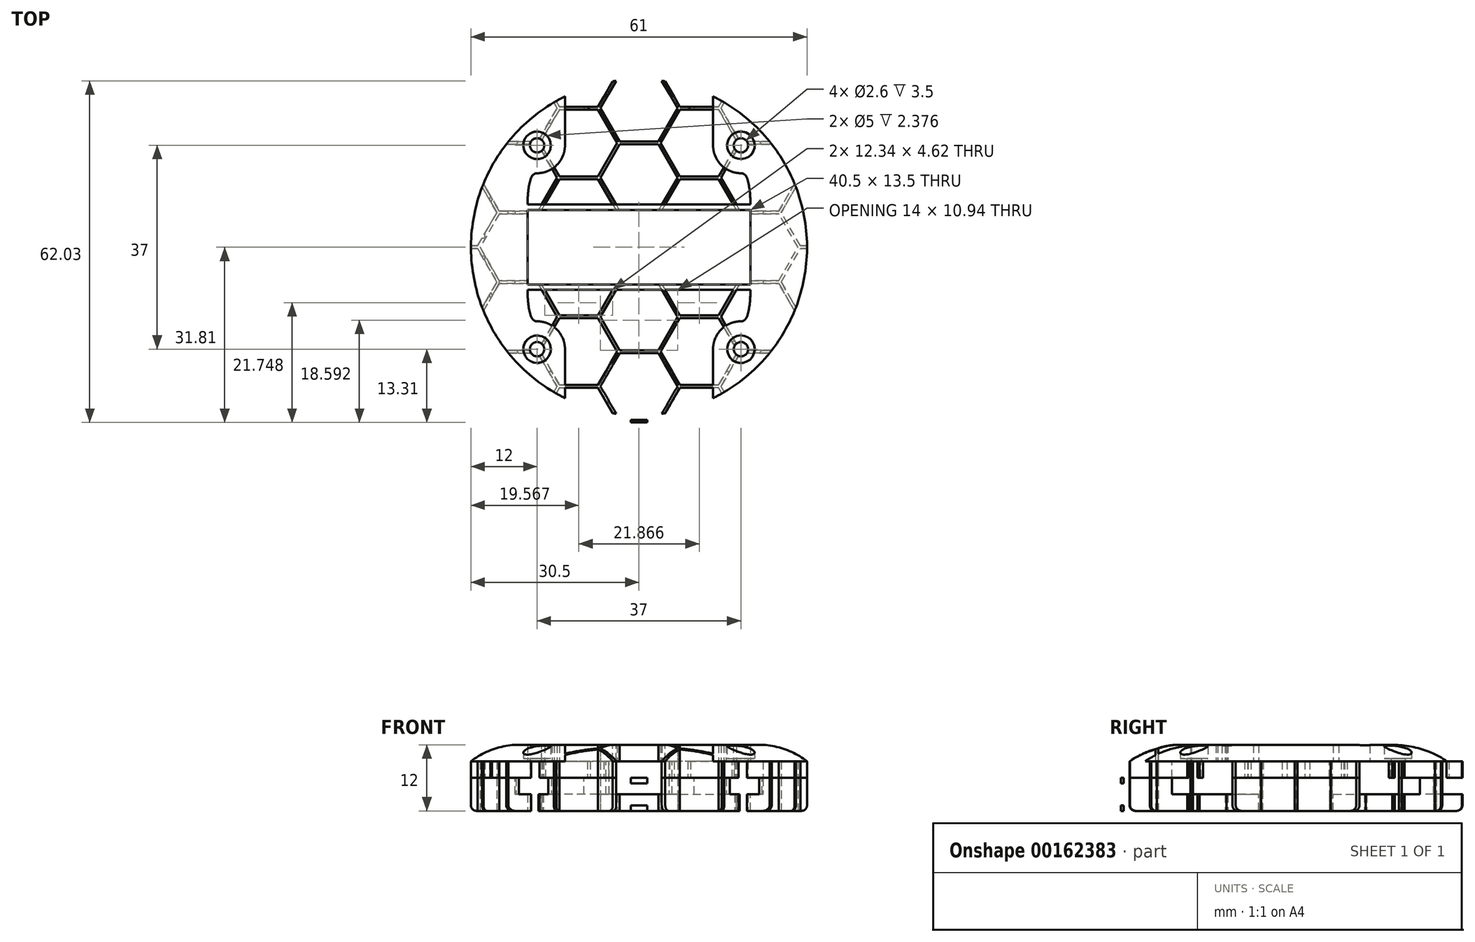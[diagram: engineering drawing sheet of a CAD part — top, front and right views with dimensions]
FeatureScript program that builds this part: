
annotation { "Feature Type Name" : "Feature", "Feature Type Description" : "" }
export const myFeature = defineFeature(function(context is Context, id is Id, definition is map)
    precondition{}
    {
        {
            var Q0;
            Q0=qCreatedBy(makeId("Top.planeOp"),FACE);
            var sketch = newSketch(context, id + "F0", { "sketchPlane" : qUnion([Q0])});
            skCircle(sketch, "E0", {"center": v(0, 0) * mm, "radius": 30.5 * mm});
            skLineSegment(sketch, "E1.bottom", {"start": v(18.5, 18.5) * mm, "end": v(-18.5, 18.5) * mm, "construction": true});
            skLineSegment(sketch, "E1.top", {"start": v(18.5, -18.5) * mm, "end": v(-18.5, -18.5) * mm, "construction": true});
            skLineSegment(sketch, "E1.left", {"start": v(18.5, 18.5) * mm, "end": v(18.5, -18.5) * mm, "construction": true});
            skLineSegment(sketch, "E1.right", {"start": v(-18.5, 18.5) * mm, "end": v(-18.5, -18.5) * mm, "construction": true});
            skCircle(sketch, "E2", {"center": v(-18.5, 18.5) * mm, "radius": 1.25 * mm});
            skCircle(sketch, "E3", {"center": v(18.5, 18.5) * mm, "radius": 1.25 * mm});
            skCircle(sketch, "E4", {"center": v(18.5, -18.5) * mm, "radius": 1.25 * mm});
            skCircle(sketch, "E5", {"center": v(-18.5, -18.5) * mm, "radius": 1.25 * mm});
            skLineSegment(sketch, "E6.bottom", {"start": v(22.5, 22.5) * mm, "end": v(-22.5, 22.5) * mm, "construction": true});
            skLineSegment(sketch, "E6.top", {"start": v(22.5, -22.5) * mm, "end": v(-22.5, -22.5) * mm, "construction": true});
            skLineSegment(sketch, "E6.left", {"start": v(22.5, 22.5) * mm, "end": v(22.5, -22.5) * mm, "construction": true});
            skLineSegment(sketch, "E6.right", {"start": v(-22.5, 22.5) * mm, "end": v(-22.5, -22.5) * mm, "construction": true});
            skLineSegment(sketch, "E7", {"start": v(-18.5, 22.5) * mm, "end": v(-22.5, 18.5) * mm});
            skLineSegment(sketch, "E8", {"start": v(-22.5, 18.5) * mm, "end": v(-22.5, -18.5) * mm});
            skLineSegment(sketch, "E9", {"start": v(-22.5, -18.5) * mm, "end": v(-18.5, -22.5) * mm});
            skLineSegment(sketch, "E10", {"start": v(-18.5, -22.5) * mm, "end": v(18.5, -22.5) * mm});
            skLineSegment(sketch, "E11", {"start": v(18.5, -22.5) * mm, "end": v(22.5, -18.5) * mm});
            skLineSegment(sketch, "E12", {"start": v(22.5, -18.5) * mm, "end": v(22.5, 18.5) * mm});
            skLineSegment(sketch, "E13", {"start": v(22.5, 18.5) * mm, "end": v(18.5, 22.5) * mm});
            skLineSegment(sketch, "E14", {"start": v(-18.5, 22.5) * mm, "end": v(18.5, 22.5) * mm});
            skLineSegment(sketch, "E15", {"start": v(-22.5, 22.5) * mm, "end": v(22.5, -22.5) * mm, "construction": true});
            skLineSegment(sketch, "E16", {"start": v(-22.5, -22.5) * mm, "end": v(22.5, 22.5) * mm, "construction": true});
            skLineSegment(sketch, "E17", {"start": v(-10, 22.5) * mm, "end": v(-10, 28.81) * mm});
            skLineSegment(sketch, "E18", {"start": v(10, 22.5) * mm, "end": v(10, 28.81) * mm});
            skSolve(sketch);
        }
        {
            var Q0;
            Q0=makeQuery(id+"F0.imprint","IMPRINT",FACE,{"disambiguationData":[TD([[makeQuery(id+"F0.imprint","IMPRINT",EDGE,{"derivedFrom":sQuery(id+"F0.wireOp",EDGE,"E2")}),-1.0]])]});
            var Q1;
            {var subQ4=sQuery(id+"F0.wireOp",EDGE,"E7");Q1=makeQuery(id+"F0.imprint","IMPRINT",FACE,{"disambiguationData":[TD([[makeQuery(id+"F0.imprint","IMPRINT",EDGE,{"derivedFrom":subQ4}),-1.0]])]});}
            var Q2;
            {var subQ0=sQuery(id+"F0.wireOp",EDGE,"E17");Q2=makeQuery(id+"F0.imprint","IMPRINT",FACE,{"disambiguationData":[TD([[makeQuery(id+"F0.imprint","IMPRINT",EDGE,{"derivedFrom":subQ0}),-1.0]])]});}
            extrude(context, id + "F1", {"entities" : qUnion([Q0, Q1, Q2]), "depth" : 3 * mm});
        }
        {
            var Q0;
            {var subQ4=sQuery(id+"F0.wireOp",EDGE,"E7");Q0=makeQuery(id+"F0.imprint","IMPRINT",FACE,{"disambiguationData":[TD([[makeQuery(id+"F0.imprint","IMPRINT",EDGE,{"derivedFrom":subQ4}),-1.0]])]});}
            extrude(context, id + "F2", {"entities" : qUnion([Q0]), "operationType" : NewBodyOperationType.ADD, "depth" : 6 * mm});
        }
        {
            var Q0;
            Q0=qCreatedBy(makeId("Right.planeOp"),FACE);
            var sketch = newSketch(context, id + "F3", { "sketchPlane" : qUnion([Q0])});
            skLineSegment(sketch, "E19.bottom", {"start": v(-29, 0) * mm, "end": v(-36.5, 0) * mm});
            skLineSegment(sketch, "E19.top", {"start": v(-29, 6) * mm, "end": v(-36.5, 6) * mm});
            skLineSegment(sketch, "E19.left", {"start": v(-29, 0) * mm, "end": v(-29, 6) * mm});
            skLineSegment(sketch, "E19.right", {"start": v(-36.5, 0) * mm, "end": v(-36.5, 6) * mm});
            skLineSegment(sketch, "E20.bottom", {"start": v(-29, 1) * mm, "end": v(-35, 1) * mm});
            skLineSegment(sketch, "E20.top", {"start": v(-29, 5) * mm, "end": v(-35, 5) * mm});
            skLineSegment(sketch, "E20.left", {"start": v(-29, 1) * mm, "end": v(-29, 5) * mm});
            skLineSegment(sketch, "E20.right", {"start": v(-35, 1) * mm, "end": v(-35, 5) * mm});
            skSolve(sketch);
        }
        {
            var Q0;
            {var subQ4=sQuery(id+"F3.wireOp",EDGE,"E19.bottom");Q0=makeQuery(id+"F3.imprint","IMPRINT",FACE,{"disambiguationData":[TD([[makeQuery(id+"F3.imprint","IMPRINT",EDGE,{"derivedFrom":subQ4}),-1.0]])]});}
            extrude(context, id + "F4", {"entities" : qUnion([Q0]), "operationType" : NewBodyOperationType.ADD, "depth" : 1.5 * mm, "hasSecondDirection" : true, "secondDirectionOppositeDirection" : true, "secondDirectionDepth" : 1.5 * mm});
        }
        {
            var Q0;
            Q0=makeQuery(id+"F1.opExtrude","CAP_EDGE",EDGE,{"disambiguationData":[OSD([sQuery(id+"F0.wireOp",EDGE,"E0")])],"isStart":true});
            fillet(context, id + "F5", {"entities" : qUnion([Q0]), "radius" : 1 * mm, "tangentPropagation" : true, "allowEdgeOverflow" : false});
        }
        {
            var Q0;
            Q0=qCreatedBy(makeId("Top.planeOp"),FACE);
            var sketch = newSketch(context, id + "F6", { "sketchPlane" : qUnion([Q0])});
            skCircle(sketch, "E21", {"center": v(0, 0) * mm, "radius": 30.5 * mm});
            skLineSegment(sketch, "E22.bottom", {"start": v(18.5, 18.5) * mm, "end": v(-18.5, 18.5) * mm, "construction": true});
            skLineSegment(sketch, "E22.top", {"start": v(18.5, -18.5) * mm, "end": v(-18.5, -18.5) * mm, "construction": true});
            skLineSegment(sketch, "E22.left", {"start": v(18.5, 18.5) * mm, "end": v(18.5, -18.5) * mm, "construction": true});
            skLineSegment(sketch, "E22.right", {"start": v(-18.5, 18.5) * mm, "end": v(-18.5, -18.5) * mm, "construction": true});
            skCircle(sketch, "E23", {"center": v(-18.5, 18.5) * mm, "radius": 1.3 * mm});
            skCircle(sketch, "E24", {"center": v(18.5, 18.5) * mm, "radius": 1.3 * mm});
            skCircle(sketch, "E25", {"center": v(18.5, -18.5) * mm, "radius": 1.3 * mm});
            skCircle(sketch, "E26", {"center": v(-18.5, -18.5) * mm, "radius": 1.3 * mm});
            skLineSegment(sketch, "E27", {"start": v(-22.5, 15.67) * mm, "end": v(-22.5, -15.67) * mm});
            skLineSegment(sketch, "E28", {"start": v(-15.67, -22.5) * mm, "end": v(15.67, -22.5) * mm});
            skLineSegment(sketch, "E29", {"start": v(22.5, -15.67) * mm, "end": v(22.5, 15.67) * mm});
            skLineSegment(sketch, "E30", {"start": v(-15.67, 22.5) * mm, "end": v(-11.25, 22.5) * mm});
            skLineSegment(sketch, "E31", {"start": v(-22.5, 22.5) * mm, "end": v(22.5, -22.5) * mm, "construction": true});
            skLineSegment(sketch, "E32", {"start": v(-22.5, -22.5) * mm, "end": v(22.5, 22.5) * mm, "construction": true});
            skLineSegment(sketch, "E33", {"start": v(22.5, -15.67) * mm, "end": v(18.5, -15.67) * mm});
            skLineSegment(sketch, "E34", {"start": v(18.5, -15.67) * mm, "end": v(15.67, -18.5) * mm});
            skLineSegment(sketch, "E35", {"start": v(15.67, -18.5) * mm, "end": v(15.67, -22.5) * mm});
            skLineSegment(sketch, "E36", {"start": v(22.5, 15.67) * mm, "end": v(18.5, 15.67) * mm});
            skLineSegment(sketch, "E37", {"start": v(18.5, 15.67) * mm, "end": v(15.67, 18.5) * mm});
            skLineSegment(sketch, "E38", {"start": v(15.67, 18.5) * mm, "end": v(15.67, 22.5) * mm});
            skLineSegment(sketch, "E39", {"start": v(-15.67, -22.5) * mm, "end": v(-15.67, -18.5) * mm});
            skLineSegment(sketch, "E40", {"start": v(-15.67, -18.5) * mm, "end": v(-18.5, -15.67) * mm});
            skLineSegment(sketch, "E41", {"start": v(-18.5, -15.67) * mm, "end": v(-22.5, -15.67) * mm});
            skLineSegment(sketch, "E42", {"start": v(-15.67, 22.5) * mm, "end": v(-15.67, 18.5) * mm});
            skLineSegment(sketch, "E43", {"start": v(-15.67, 18.5) * mm, "end": v(-18.5, 15.67) * mm});
            skLineSegment(sketch, "E44", {"start": v(-18.5, 15.67) * mm, "end": v(-22.5, 15.67) * mm});
            skLineSegment(sketch, "E45.bottom", {"start": v(-20.25, -6.75) * mm, "end": v(20.25, -6.75) * mm});
            skLineSegment(sketch, "E45.top", {"start": v(-20.25, 6.75) * mm, "end": v(20.25, 6.75) * mm});
            skLineSegment(sketch, "E45.left", {"start": v(-20.25, -6.75) * mm, "end": v(-20.25, 6.75) * mm});
            skLineSegment(sketch, "E45.right", {"start": v(20.25, -6.75) * mm, "end": v(20.25, 6.75) * mm});
            skLineSegment(sketch, "E46.bottom", {"start": v(-22.5, -22.5) * mm, "end": v(22.5, -22.5) * mm, "construction": true});
            skLineSegment(sketch, "E46.left", {"start": v(-22.5, -22.5) * mm, "end": v(-22.5, 22.5) * mm, "construction": true});
            skLineSegment(sketch, "E46.right", {"start": v(22.5, -22.5) * mm, "end": v(22.5, 22.5) * mm, "construction": true});
            skArc(sketch, "E47", {"start": v(11.25, 22.5) * mm, "mid": v(0, 29) * mm, "end": v(-11.25, 22.5) * mm});
            skPoint(sketch, "E48", {"position": v(0, 18.5) * mm});
            skLineSegment(sketch, "E49.trimOffspring", {"start": v(11.25, 22.5) * mm, "end": v(15.67, 22.5) * mm});
            skCircle(sketch, "E50", {"center": v(18.5, 18.5) * mm, "radius": 2.5 * mm});
            skCircle(sketch, "E51", {"center": v(-18.5, 18.5) * mm, "radius": 2.5 * mm});
            skCircle(sketch, "E52", {"center": v(-18.5, -18.5) * mm, "radius": 2.5 * mm});
            skCircle(sketch, "E53", {"center": v(18.5, -18.5) * mm, "radius": 2.5 * mm});
            skLineSegment(sketch, "E54.bottom", {"start": v(-30.43, -2) * mm, "end": v(-28.43, -2) * mm});
            skLineSegment(sketch, "E54.top", {"start": v(-30.43, 2) * mm, "end": v(-28.43, 2) * mm});
            skPoint(sketch, "E54.middle", {"position": v(-28.43, 0) * mm});
            skPoint(sketch, "E54.middle.positionSnap0", {"position": v(-20.25, 0) * mm});
            skPoint(sketch, "E54.centerSnap0", {"position": v(-20.25, 0) * mm});
            skArc(sketch, "E55", {"start": v(-28.43, -2) * mm, "mid": v(-27.85, -6.06) * mm, "end": v(-26.69, -10) * mm});
            skArc(sketch, "E56", {"start": v(-28.43, 2) * mm, "mid": v(-27.45, 7.66) * mm, "end": v(-25.36, 13) * mm});
            skLineSegment(sketch, "E57", {"start": v(-25.36, 13) * mm, "end": v(-22.5, 13) * mm});
            skLineSegment(sketch, "E58", {"start": v(-22.5, 13) * mm, "end": v(-22.5, 10.14) * mm});
            skLineSegment(sketch, "E59", {"start": v(-22.5, 12.8) * mm, "end": v(-25.02, 12.8) * mm});
            skArc(sketch, "E60", {"start": v(-25.02, 12.8) * mm, "mid": v(-28.06, 1.53) * mm, "end": v(-26.26, -10) * mm});
            skLineSegment(sketch, "E61", {"start": v(-26.69, -10) * mm, "end": v(-26.26, -10) * mm});
            skLineSegment(sketch, "E62", {"start": v(-28.05, -1.6) * mm, "end": v(-31.71, -1.6) * mm});
            skLineSegment(sketch, "E63", {"start": v(-28.05, 1.6) * mm, "end": v(-31.71, 1.6) * mm});
            skArc(sketch, "E64", {"start": v(-31.71, -1.6) * mm, "mid": v(-33.31, 0) * mm, "end": v(-31.71, 1.6) * mm});
            skArc(sketch, "E65", {"start": v(-22.5, 10.14) * mm, "mid": v(-25.08, 0.24) * mm, "end": v(-25.14, -10) * mm});
            skLineSegment(sketch, "E66", {"start": v(-25.14, -10) * mm, "end": v(-22.5, -10) * mm});
            skSolve(sketch);
        }
        {
            var Q0;
            Q0=makeQuery(id+"F6.imprint","IMPRINT",FACE,{"disambiguationData":[TD([[makeQuery(id+"F6.imprint","IMPRINT",EDGE,{"derivedFrom":sQuery(id+"F6.wireOp",EDGE,"E21")}),1.0]])]});
            var Q1;
            Q1=makeQuery(id+"F6.imprint","IMPRINT",FACE,{"disambiguationData":[TD([[makeQuery(id+"F6.imprint","IMPRINT",EDGE,{"derivedFrom":sQuery(id+"F6.wireOp",EDGE,"E25")}),-1.0]])]});
            var Q2;
            Q2=makeQuery(id+"F6.imprint","IMPRINT",FACE,{"disambiguationData":[TD([[makeQuery(id+"F6.imprint","IMPRINT",EDGE,{"derivedFrom":sQuery(id+"F6.wireOp",EDGE,"E26")}),-1.0]])]});
            var Q3;
            Q3=makeQuery(id+"F6.imprint","IMPRINT",FACE,{"disambiguationData":[TD([[makeQuery(id+"F6.imprint","IMPRINT",EDGE,{"derivedFrom":sQuery(id+"F6.wireOp",EDGE,"E23")}),-1.0]])]});
            var Q4;
            Q4=makeQuery(id+"F6.imprint","IMPRINT",FACE,{"disambiguationData":[TD([[makeQuery(id+"F6.imprint","IMPRINT",EDGE,{"derivedFrom":sQuery(id+"F6.wireOp",EDGE,"E24")}),-1.0]])]});
            var Q5;
            {var subQ5=sQuery(id+"F6.wireOp",EDGE,"E64");Q5=makeQuery(id+"F6.imprint","IMPRINT",FACE,{"disambiguationData":[TD([[makeQuery(id+"F6.imprint","IMPRINT",EDGE,{"derivedFrom":subQ5}),-1.0]])]});}
            var Q6;
            Q6=makeQuery(id+"F6.imprint","IMPRINT",FACE,{"disambiguationData":[TD([[makeQuery(id+"F6.imprint","IMPRINT",EDGE,{"derivedFrom":sQuery(id+"F6.wireOp",EDGE,"E28")}),-1.0]])]});
            extrude(context, id + "F7", {"entities" : qUnion([Q0, Q1, Q2, Q3, Q4, Q5, Q6]), "depth" : 9 * mm, "hasSecondDirection" : true, "secondDirectionOppositeDirection" : false, "secondDirectionDepth" : 6 * mm});
        }
        {
            var Q0;
            Q0=qCreatedBy(makeId("Right.planeOp"),FACE);
            var sketch = newSketch(context, id + "F8", { "sketchPlane" : qUnion([Q0])});
            skLineSegment(sketch, "E67", {"start": v(30.5, 9) * mm, "end": v(30.5, 19.06) * mm});
            skLineSegment(sketch, "E68", {"start": v(30.5, 19.06) * mm, "end": v(-30.5, 19.06) * mm});
            skLineSegment(sketch, "E69", {"start": v(-30.5, 19.06) * mm, "end": v(-30.5, 9) * mm});
            skArc(sketch, "E70", {"start": v(30.5, 9) * mm, "mid": v(26.39, 11.23) * mm, "end": v(21.77, 12) * mm});
            skArc(sketch, "E71.MirrorCS", {"start": v(-30.5, 9) * mm, "mid": v(-26.39, 11.23) * mm, "end": v(-21.77, 12) * mm});
            skLineSegment(sketch, "E72", {"start": v(-21.77, 12) * mm, "end": v(21.77, 12) * mm});
            skLineSegment(sketch, "E73", {"start": v(0, 12) * mm, "end": v(0, 19.06) * mm});
            skSolve(sketch);
        }
        {
            var Q0;
            Q0=qCreatedBy(makeId("Top.planeOp"),FACE);
            var sketch = newSketch(context, id + "F9", { "sketchPlane" : qUnion([Q0])});
            skLineSegment(sketch, "E74", {"start": v(20.25, 6.75) * mm, "end": v(20.25, -6.75) * mm});
            skCircle(sketch, "E75", {"center": v(0, 0) * mm, "radius": 30.5 * mm});
            skLineSegment(sketch, "E76.bottom", {"start": v(-18.5, -18.5) * mm, "end": v(18.5, -18.5) * mm, "construction": true});
            skLineSegment(sketch, "E76.top", {"start": v(-18.5, 18.5) * mm, "end": v(18.5, 18.5) * mm, "construction": true});
            skLineSegment(sketch, "E76.left", {"start": v(-18.5, -18.5) * mm, "end": v(-18.5, 18.5) * mm, "construction": true});
            skLineSegment(sketch, "E76.right", {"start": v(18.5, -18.5) * mm, "end": v(18.5, 18.5) * mm, "construction": true});
            skLineSegment(sketch, "E77", {"start": v(18.5, -18.5) * mm, "end": v(-18.5, 18.5) * mm, "construction": true});
            skLineSegment(sketch, "E78", {"start": v(18.5, 18.5) * mm, "end": v(-18.5, -18.5) * mm, "construction": true});
            skCircle(sketch, "E79", {"center": v(18.5, -18.5) * mm, "radius": 5.06 * mm, "construction": true});
            skFitSpline(sketch, "E80", {"points": [v(20.25, -6.75) * mm, v(19.9, -11.5) * mm, v(18.5, -13.44) * mm], "startDerivative": vector(0, -9.06) * mm, "endDerivative": vector(-6.35, 0) * mm});
            skLineSegment(sketch, "E81", {"start": v(13.44, -18.5) * mm, "end": v(13.44, -27.38) * mm});
            skArc(sketch, "E82", {"start": v(18.5, -13.44) * mm, "mid": v(14.92, -14.92) * mm, "end": v(13.44, -18.5) * mm});
            skArc(sketch, "E83.MirrorCS", {"start": v(18.5, 13.44) * mm, "mid": v(14.92, 14.92) * mm, "end": v(13.44, 18.5) * mm});
            skFitSpline(sketch, "E84.MirrorCS", {"points": [v(20.25, 6.75) * mm, v(19.9, 11.5) * mm, v(18.5, 13.44) * mm], "startDerivative": vector(0, 9.06) * mm, "endDerivative": vector(-6.35, 0) * mm});
            skLineSegment(sketch, "E85", {"start": v(13.44, 18.5) * mm, "end": v(13.44, 27.38) * mm});
            skLineSegment(sketch, "E86.MirrorCS", {"start": v(-13.44, -18.5) * mm, "end": v(-13.44, -27.38) * mm});
            skArc(sketch, "E87.MirrorCS", {"start": v(-18.5, -13.44) * mm, "mid": v(-14.92, -14.92) * mm, "end": v(-13.44, -18.5) * mm});
            skFitSpline(sketch, "E88.MirrorCS", {"points": [v(-20.25, -6.75) * mm, v(-19.9, -11.5) * mm, v(-18.5, -13.44) * mm], "startDerivative": vector(0, -9.06) * mm, "endDerivative": vector(6.35, 0) * mm});
            skLineSegment(sketch, "E89.MirrorCS", {"start": v(-13.44, 18.5) * mm, "end": v(-13.44, 27.38) * mm});
            skLineSegment(sketch, "E90.MirrorCS", {"start": v(-20.25, 6.75) * mm, "end": v(-20.25, -6.75) * mm});
            skFitSpline(sketch, "E91.MirrorCS", {"points": [v(-20.25, 6.75) * mm, v(-19.9, 11.5) * mm, v(-18.5, 13.44) * mm], "startDerivative": vector(0, 9.06) * mm, "endDerivative": vector(6.35, 0) * mm});
            skArc(sketch, "E92.MirrorCS", {"start": v(-18.5, 13.44) * mm, "mid": v(-14.92, 14.92) * mm, "end": v(-13.44, 18.5) * mm});
            skLineSegment(sketch, "E93", {"start": v(20.25, 6.75) * mm, "end": v(-20.25, 6.75) * mm});
            skLineSegment(sketch, "E94", {"start": v(-20.25, -6.75) * mm, "end": v(20.25, -6.75) * mm});
            skLineSegment(sketch, "E95", {"start": v(20.24, -7.75) * mm, "end": v(-20.24, -7.75) * mm});
            skLineSegment(sketch, "E96", {"start": v(-20.24, 7.75) * mm, "end": v(20.25, 7.75) * mm});
            skSolve(sketch);
        }
        {
            var Q0;
            Q0=qCreatedBy(makeId("Top.planeOp"),FACE);
            var sketch = newSketch(context, id + "F10", { "sketchPlane" : qUnion([Q0])});
            skCircle(sketch, "E97.cCircle", {"center": v(0, 0) * mm, "radius": 7 * mm, "construction": true});
            skLineSegment(sketch, "E97.0", {"start": v(-7, 0) * mm, "end": v(-3.5, 6.06) * mm});
            skLineSegment(sketch, "E97.1", {"start": v(-3.5, 6.06) * mm, "end": v(3.5, 6.06) * mm});
            skLineSegment(sketch, "E97.2", {"start": v(3.5, 6.06) * mm, "end": v(7, 0) * mm});
            skLineSegment(sketch, "E97.3", {"start": v(7, 0) * mm, "end": v(3.5, -6.06) * mm});
            skLineSegment(sketch, "E97.4", {"start": v(3.5, -6.06) * mm, "end": v(-3.5, -6.06) * mm});
            skLineSegment(sketch, "E97.5", {"start": v(-3.5, -6.06) * mm, "end": v(-7, 0) * mm});
            skLineSegment(sketch, "E98.0.1.0", {"start": v(-3.5, 18.69) * mm, "end": v(3.5, 18.69) * mm});
            skLineSegment(sketch, "E98.0.1.1", {"start": v(3.5, 6.56) * mm, "end": v(-3.5, 6.56) * mm});
            skLineSegment(sketch, "E98.0.1.2", {"start": v(-3.5, 6.56) * mm, "end": v(-7, 12.62) * mm});
            skLineSegment(sketch, "E98.0.1.3", {"start": v(-7, 12.62) * mm, "end": v(-3.5, 18.69) * mm});
            skLineSegment(sketch, "E98.0.1.4", {"start": v(3.5, 18.69) * mm, "end": v(7, 12.62) * mm});
            skLineSegment(sketch, "E98.0.1.5", {"start": v(7, 12.62) * mm, "end": v(3.5, 6.56) * mm});
            skLineSegment(sketch, "E98.0.2.0", {"start": v(-3.5, 31.31) * mm, "end": v(3.5, 31.31) * mm});
            skLineSegment(sketch, "E98.0.2.1", {"start": v(3.5, 19.19) * mm, "end": v(-3.5, 19.19) * mm});
            skLineSegment(sketch, "E98.0.2.2", {"start": v(-3.5, 19.19) * mm, "end": v(-7, 25.25) * mm});
            skLineSegment(sketch, "E98.0.2.3", {"start": v(-7, 25.25) * mm, "end": v(-3.5, 31.31) * mm});
            skLineSegment(sketch, "E98.0.2.4", {"start": v(3.5, 31.31) * mm, "end": v(7, 25.25) * mm});
            skLineSegment(sketch, "E98.0.2.5", {"start": v(7, 25.25) * mm, "end": v(3.5, 19.19) * mm});
            skLineSegment(sketch, "E98.0.3.0", {"start": v(-3.5, 43.94) * mm, "end": v(3.5, 43.94) * mm});
            skLineSegment(sketch, "E98.0.3.1", {"start": v(3.5, 31.81) * mm, "end": v(-3.5, 31.81) * mm});
            skLineSegment(sketch, "E98.0.3.2", {"start": v(-3.5, 31.81) * mm, "end": v(-7, 37.87) * mm});
            skLineSegment(sketch, "E98.0.3.3", {"start": v(-7, 37.87) * mm, "end": v(-3.5, 43.94) * mm});
            skLineSegment(sketch, "E98.0.3.4", {"start": v(3.5, 43.94) * mm, "end": v(7, 37.87) * mm});
            skLineSegment(sketch, "E98.0.3.5", {"start": v(7, 37.87) * mm, "end": v(3.5, 31.81) * mm});
            skLineSegment(sketch, "E98.direction1", {"start": v(-2.6, -6.06) * mm, "end": v(-3.5, -6.06) * mm, "construction": true});
            skLineSegment(sketch, "E98.direction2", {"start": v(-3.5, -6.06) * mm, "end": v(-3.5, 6.56) * mm, "construction": true});
            skLineSegment(sketch, "E99.0.1.0", {"start": v(3.5, -6.56) * mm, "end": v(7, -12.62) * mm});
            skLineSegment(sketch, "E99.0.1.1", {"start": v(7, -12.62) * mm, "end": v(3.5, -18.69) * mm});
            skLineSegment(sketch, "E99.0.1.2", {"start": v(-3.5, -6.56) * mm, "end": v(3.5, -6.56) * mm});
            skLineSegment(sketch, "E99.0.1.3", {"start": v(-7, -12.62) * mm, "end": v(-3.5, -6.56) * mm});
            skLineSegment(sketch, "E99.0.1.4", {"start": v(3.5, -18.69) * mm, "end": v(-3.5, -18.69) * mm});
            skLineSegment(sketch, "E99.0.1.5", {"start": v(-3.5, -18.69) * mm, "end": v(-7, -12.62) * mm});
            skLineSegment(sketch, "E99.0.1.6", {"start": v(-2.6, -18.69) * mm, "end": v(-3.5, -18.69) * mm, "construction": true});
            skLineSegment(sketch, "E99.0.2.0", {"start": v(3.5, -19.19) * mm, "end": v(7, -25.25) * mm});
            skLineSegment(sketch, "E99.0.2.1", {"start": v(7, -25.25) * mm, "end": v(3.5, -31.31) * mm});
            skLineSegment(sketch, "E99.0.2.2", {"start": v(-3.5, -19.19) * mm, "end": v(3.5, -19.19) * mm});
            skLineSegment(sketch, "E99.0.2.3", {"start": v(-7, -25.25) * mm, "end": v(-3.5, -19.19) * mm});
            skLineSegment(sketch, "E99.0.2.4", {"start": v(3.5, -31.31) * mm, "end": v(-3.5, -31.31) * mm});
            skLineSegment(sketch, "E99.0.2.5", {"start": v(-3.5, -31.31) * mm, "end": v(-7, -25.25) * mm});
            skLineSegment(sketch, "E99.0.2.6", {"start": v(-2.6, -31.31) * mm, "end": v(-3.5, -31.31) * mm, "construction": true});
            skLineSegment(sketch, "E99.0.3.0", {"start": v(3.5, -31.81) * mm, "end": v(7, -37.87) * mm});
            skLineSegment(sketch, "E99.0.3.1", {"start": v(7, -37.87) * mm, "end": v(3.5, -43.94) * mm});
            skLineSegment(sketch, "E99.0.3.2", {"start": v(-3.5, -31.81) * mm, "end": v(3.5, -31.81) * mm});
            skLineSegment(sketch, "E99.0.3.3", {"start": v(-7, -37.87) * mm, "end": v(-3.5, -31.81) * mm});
            skLineSegment(sketch, "E99.0.3.4", {"start": v(3.5, -43.94) * mm, "end": v(-3.5, -43.94) * mm});
            skLineSegment(sketch, "E99.0.3.5", {"start": v(-3.5, -43.94) * mm, "end": v(-7, -37.87) * mm});
            skLineSegment(sketch, "E99.0.3.6", {"start": v(-2.6, -43.94) * mm, "end": v(-3.5, -43.94) * mm, "construction": true});
            skLineSegment(sketch, "E99.direction1", {"start": v(-2.6, -6.06) * mm, "end": v(-2.7, -6.06) * mm, "construction": true});
            skLineSegment(sketch, "E99.direction2", {"start": v(-2.6, -6.06) * mm, "end": v(-2.6, -18.69) * mm, "construction": true});
            skCircle(sketch, "E100.cCircle", {"center": v(10.93, -44.19) * mm, "radius": 7 * mm, "construction": true});
            skLineSegment(sketch, "E100.0", {"start": v(3.93, -44.19) * mm, "end": v(7.43, -38.12) * mm});
            skLineSegment(sketch, "E100.1", {"start": v(7.43, -38.12) * mm, "end": v(14.43, -38.12) * mm});
            skLineSegment(sketch, "E100.2", {"start": v(14.43, -38.12) * mm, "end": v(17.93, -44.19) * mm});
            skLineSegment(sketch, "E100.3", {"start": v(17.93, -44.19) * mm, "end": v(14.43, -50.25) * mm});
            skLineSegment(sketch, "E100.4", {"start": v(14.43, -50.25) * mm, "end": v(7.43, -50.25) * mm});
            skLineSegment(sketch, "E100.5", {"start": v(7.43, -50.25) * mm, "end": v(3.93, -44.19) * mm});
            skLineSegment(sketch, "E101.0.1.0", {"start": v(3.93, -31.56) * mm, "end": v(7.43, -25.5) * mm});
            skLineSegment(sketch, "E101.0.1.1", {"start": v(17.93, -31.56) * mm, "end": v(14.43, -37.62) * mm});
            skLineSegment(sketch, "E101.0.1.2", {"start": v(7.43, -25.5) * mm, "end": v(14.43, -25.5) * mm});
            skLineSegment(sketch, "E101.0.1.3", {"start": v(14.43, -25.5) * mm, "end": v(17.93, -31.56) * mm});
            skLineSegment(sketch, "E101.0.1.4", {"start": v(14.43, -37.62) * mm, "end": v(7.43, -37.62) * mm});
            skLineSegment(sketch, "E101.0.1.5", {"start": v(7.43, -37.62) * mm, "end": v(3.93, -31.56) * mm});
            skLineSegment(sketch, "E101.0.2.0", {"start": v(3.93, -18.94) * mm, "end": v(7.43, -12.87) * mm});
            skLineSegment(sketch, "E101.0.2.1", {"start": v(17.93, -18.94) * mm, "end": v(14.43, -25) * mm});
            skLineSegment(sketch, "E101.0.2.2", {"start": v(7.43, -12.87) * mm, "end": v(14.43, -12.87) * mm});
            skLineSegment(sketch, "E101.0.2.3", {"start": v(14.43, -12.87) * mm, "end": v(17.93, -18.94) * mm});
            skLineSegment(sketch, "E101.0.2.4", {"start": v(14.43, -25) * mm, "end": v(7.43, -25) * mm});
            skLineSegment(sketch, "E101.0.2.5", {"start": v(7.43, -25) * mm, "end": v(3.93, -18.94) * mm});
            skLineSegment(sketch, "E101.0.3.0", {"start": v(3.93, -6.31) * mm, "end": v(7.43, -0.25) * mm});
            skLineSegment(sketch, "E101.0.3.1", {"start": v(17.93, -6.31) * mm, "end": v(14.43, -12.37) * mm});
            skLineSegment(sketch, "E101.0.3.2", {"start": v(7.43, -0.25) * mm, "end": v(14.43, -0.25) * mm});
            skLineSegment(sketch, "E101.0.3.3", {"start": v(14.43, -0.25) * mm, "end": v(17.93, -6.31) * mm});
            skLineSegment(sketch, "E101.0.3.4", {"start": v(14.43, -12.37) * mm, "end": v(7.43, -12.37) * mm});
            skLineSegment(sketch, "E101.0.3.5", {"start": v(7.43, -12.37) * mm, "end": v(3.93, -6.31) * mm});
            skLineSegment(sketch, "E101.0.4.0", {"start": v(3.93, 6.31) * mm, "end": v(7.43, 12.37) * mm});
            skLineSegment(sketch, "E101.0.4.1", {"start": v(17.93, 6.31) * mm, "end": v(14.43, 0.25) * mm});
            skLineSegment(sketch, "E101.0.4.2", {"start": v(7.43, 12.37) * mm, "end": v(14.43, 12.37) * mm});
            skLineSegment(sketch, "E101.0.4.3", {"start": v(14.43, 12.37) * mm, "end": v(17.93, 6.31) * mm});
            skLineSegment(sketch, "E101.0.4.4", {"start": v(14.43, 0.25) * mm, "end": v(7.43, 0.25) * mm});
            skLineSegment(sketch, "E101.0.4.5", {"start": v(7.43, 0.25) * mm, "end": v(3.93, 6.31) * mm});
            skLineSegment(sketch, "E101.0.5.0", {"start": v(3.93, 18.94) * mm, "end": v(7.43, 25) * mm});
            skLineSegment(sketch, "E101.0.5.1", {"start": v(17.93, 18.94) * mm, "end": v(14.43, 12.87) * mm});
            skLineSegment(sketch, "E101.0.5.2", {"start": v(7.43, 25) * mm, "end": v(14.43, 25) * mm});
            skLineSegment(sketch, "E101.0.5.3", {"start": v(14.43, 25) * mm, "end": v(17.93, 18.94) * mm});
            skLineSegment(sketch, "E101.0.5.4", {"start": v(14.43, 12.87) * mm, "end": v(7.43, 12.87) * mm});
            skLineSegment(sketch, "E101.0.5.5", {"start": v(7.43, 12.87) * mm, "end": v(3.93, 18.94) * mm});
            skLineSegment(sketch, "E101.0.6.0", {"start": v(3.93, 31.56) * mm, "end": v(7.43, 37.62) * mm});
            skLineSegment(sketch, "E101.0.6.1", {"start": v(17.93, 31.56) * mm, "end": v(14.43, 25.5) * mm});
            skLineSegment(sketch, "E101.0.6.2", {"start": v(7.43, 37.62) * mm, "end": v(14.43, 37.62) * mm});
            skLineSegment(sketch, "E101.0.6.3", {"start": v(14.43, 37.62) * mm, "end": v(17.93, 31.56) * mm});
            skLineSegment(sketch, "E101.0.6.4", {"start": v(14.43, 25.5) * mm, "end": v(7.43, 25.5) * mm});
            skLineSegment(sketch, "E101.0.6.5", {"start": v(7.43, 25.5) * mm, "end": v(3.93, 31.56) * mm});
            skLineSegment(sketch, "E101.0.7.0", {"start": v(3.93, 44.19) * mm, "end": v(7.43, 50.25) * mm});
            skLineSegment(sketch, "E101.0.7.1", {"start": v(17.93, 44.19) * mm, "end": v(14.43, 38.12) * mm});
            skLineSegment(sketch, "E101.0.7.2", {"start": v(7.43, 50.25) * mm, "end": v(14.43, 50.25) * mm});
            skLineSegment(sketch, "E101.0.7.3", {"start": v(14.43, 50.25) * mm, "end": v(17.93, 44.19) * mm});
            skLineSegment(sketch, "E101.0.7.4", {"start": v(14.43, 38.12) * mm, "end": v(7.43, 38.12) * mm});
            skLineSegment(sketch, "E101.0.7.5", {"start": v(7.43, 38.12) * mm, "end": v(3.93, 44.19) * mm});
            skLineSegment(sketch, "E101.direction1", {"start": v(0.95, -50.25) * mm, "end": v(7.43, -50.25) * mm, "construction": true});
            skLineSegment(sketch, "E101.direction2", {"start": v(7.43, -50.25) * mm, "end": v(7.43, -37.62) * mm, "construction": true});
            skLineSegment(sketch, "E102.MirrorCS", {"start": v(-14.43, -37.62) * mm, "end": v(-7.43, -37.62) * mm});
            skLineSegment(sketch, "E103.MirrorCS", {"start": v(-14.43, 0.25) * mm, "end": v(-7.43, 0.25) * mm});
            skLineSegment(sketch, "E104.MirrorCS", {"start": v(-17.93, -31.56) * mm, "end": v(-14.43, -37.62) * mm});
            skLineSegment(sketch, "E105.MirrorCS", {"start": v(-7.43, 37.62) * mm, "end": v(-14.43, 37.62) * mm});
            skLineSegment(sketch, "E106.MirrorCS", {"start": v(-14.43, -12.37) * mm, "end": v(-7.43, -12.37) * mm});
            skLineSegment(sketch, "E107.MirrorCS", {"start": v(-3.93, -31.56) * mm, "end": v(-7.43, -25.5) * mm});
            skLineSegment(sketch, "E108.MirrorCS", {"start": v(-14.43, -0.25) * mm, "end": v(-17.93, -6.31) * mm});
            skLineSegment(sketch, "E109.MirrorCS", {"start": v(-17.93, 31.56) * mm, "end": v(-14.43, 25.5) * mm});
            skLineSegment(sketch, "E110.MirrorCS", {"start": v(-7.43, -50.25) * mm, "end": v(-3.93, -44.19) * mm});
            skLineSegment(sketch, "E111.MirrorCS", {"start": v(-7.43, -0.25) * mm, "end": v(-14.43, -0.25) * mm});
            skLineSegment(sketch, "E112.MirrorCS", {"start": v(-3.93, 31.56) * mm, "end": v(-7.43, 37.62) * mm});
            skLineSegment(sketch, "E113.MirrorCS", {"start": v(-14.43, -50.25) * mm, "end": v(-7.43, -50.25) * mm});
            skLineSegment(sketch, "E114.MirrorCS", {"start": v(-17.93, -6.31) * mm, "end": v(-14.43, -12.37) * mm});
            skLineSegment(sketch, "E115.MirrorCS", {"start": v(-17.93, -44.19) * mm, "end": v(-14.43, -50.25) * mm});
            skLineSegment(sketch, "E116.MirrorCS", {"start": v(-7.43, 12.87) * mm, "end": v(-3.93, 18.94) * mm});
            skLineSegment(sketch, "E117.MirrorCS", {"start": v(-14.43, -38.12) * mm, "end": v(-17.93, -44.19) * mm});
            skLineSegment(sketch, "E118.MirrorCS", {"start": v(-14.43, 12.87) * mm, "end": v(-7.43, 12.87) * mm});
            skLineSegment(sketch, "E119.MirrorCS", {"start": v(-3.93, -6.31) * mm, "end": v(-7.43, -0.25) * mm});
            skLineSegment(sketch, "E120.MirrorCS", {"start": v(-7.43, -38.12) * mm, "end": v(-14.43, -38.12) * mm});
            skLineSegment(sketch, "E121.MirrorCS", {"start": v(-7.43, -25) * mm, "end": v(-3.93, -18.94) * mm});
            skLineSegment(sketch, "E122.MirrorCS", {"start": v(-14.43, 25) * mm, "end": v(-17.93, 18.94) * mm});
            skLineSegment(sketch, "E123.MirrorCS", {"start": v(-7.43, 0.25) * mm, "end": v(-3.93, 6.31) * mm});
            skLineSegment(sketch, "E124.MirrorCS", {"start": v(-17.93, -18.94) * mm, "end": v(-14.43, -25) * mm});
            skLineSegment(sketch, "E125.MirrorCS", {"start": v(-14.43, 50.25) * mm, "end": v(-17.93, 44.19) * mm});
            skLineSegment(sketch, "E126.MirrorCS", {"start": v(-14.43, -25.5) * mm, "end": v(-17.93, -31.56) * mm});
            skLineSegment(sketch, "E127.MirrorCS", {"start": v(-14.43, 38.12) * mm, "end": v(-7.43, 38.12) * mm});
            skLineSegment(sketch, "E128.MirrorCS", {"start": v(-7.43, -12.87) * mm, "end": v(-14.43, -12.87) * mm});
            skLineSegment(sketch, "E129.MirrorCS", {"start": v(-14.43, 25.5) * mm, "end": v(-7.43, 25.5) * mm});
            skLineSegment(sketch, "E130.MirrorCS", {"start": v(-17.93, 6.31) * mm, "end": v(-14.43, 0.25) * mm});
            skLineSegment(sketch, "E131.MirrorCS", {"start": v(-3.93, 18.94) * mm, "end": v(-7.43, 25) * mm});
            skLineSegment(sketch, "E132.MirrorCS", {"start": v(-3.93, 6.31) * mm, "end": v(-7.43, 12.37) * mm});
            skLineSegment(sketch, "E133.MirrorCS", {"start": v(-7.43, 50.25) * mm, "end": v(-14.43, 50.25) * mm});
            skLineSegment(sketch, "E134.MirrorCS", {"start": v(-17.93, 44.19) * mm, "end": v(-14.43, 38.12) * mm});
            skLineSegment(sketch, "E135.MirrorCS", {"start": v(-7.43, -37.62) * mm, "end": v(-3.93, -31.56) * mm});
            skLineSegment(sketch, "E136.MirrorCS", {"start": v(-7.43, 38.12) * mm, "end": v(-3.93, 44.19) * mm});
            skLineSegment(sketch, "E137.MirrorCS", {"start": v(-7.43, 12.37) * mm, "end": v(-14.43, 12.37) * mm});
            skLineSegment(sketch, "E138.MirrorCS", {"start": v(-17.93, 18.94) * mm, "end": v(-14.43, 12.87) * mm});
            skLineSegment(sketch, "E139.MirrorCS", {"start": v(-7.43, -12.37) * mm, "end": v(-3.93, -6.31) * mm});
            skLineSegment(sketch, "E140.MirrorCS", {"start": v(-14.43, -12.87) * mm, "end": v(-17.93, -18.94) * mm});
            skLineSegment(sketch, "E141.MirrorCS", {"start": v(-14.43, 12.37) * mm, "end": v(-17.93, 6.31) * mm});
            skLineSegment(sketch, "E142.MirrorCS", {"start": v(-3.93, -18.94) * mm, "end": v(-7.43, -12.87) * mm});
            skLineSegment(sketch, "E143.MirrorCS", {"start": v(-14.43, 37.62) * mm, "end": v(-17.93, 31.56) * mm});
            skLineSegment(sketch, "E144.MirrorCS", {"start": v(-7.43, 25) * mm, "end": v(-14.43, 25) * mm});
            skLineSegment(sketch, "E145.MirrorCS", {"start": v(-7.43, 25.5) * mm, "end": v(-3.93, 31.56) * mm});
            skLineSegment(sketch, "E146.MirrorCS", {"start": v(-14.43, -25) * mm, "end": v(-7.43, -25) * mm});
            skLineSegment(sketch, "E147.MirrorCS", {"start": v(-3.93, -44.19) * mm, "end": v(-7.43, -38.12) * mm});
            skLineSegment(sketch, "E148.MirrorCS", {"start": v(-7.43, -25.5) * mm, "end": v(-14.43, -25.5) * mm});
            skLineSegment(sketch, "E149.MirrorCS", {"start": v(-3.93, 44.19) * mm, "end": v(-7.43, 50.25) * mm});
            skLineSegment(sketch, "E150", {"start": v(-10.93, -52.39) * mm, "end": v(-10.93, 52.15) * mm, "construction": true});
            skPoint(sketch, "E150.startSnap0", {"position": v(-10.93, -50.25) * mm});
            skPoint(sketch, "E150.endSnap0", {"position": v(-10.93, 50.25) * mm});
            skLineSegment(sketch, "E151.MirrorCS", {"start": v(-19.27, -6.06) * mm, "end": v(-19.17, -6.06) * mm, "construction": true});
            skLineSegment(sketch, "E152.MirrorCS", {"start": v(-19.27, -6.06) * mm, "end": v(-18.37, -6.06) * mm, "construction": true});
            skLineSegment(sketch, "E153.MirrorCS", {"start": v(-19.27, -18.69) * mm, "end": v(-18.37, -18.69) * mm, "construction": true});
            skLineSegment(sketch, "E154.MirrorCS", {"start": v(-19.27, -31.31) * mm, "end": v(-18.37, -31.31) * mm, "construction": true});
            skLineSegment(sketch, "E155.MirrorCS", {"start": v(-19.27, -43.94) * mm, "end": v(-18.37, -43.94) * mm, "construction": true});
            skLineSegment(sketch, "E156.MirrorCS", {"start": v(-18.37, -6.56) * mm, "end": v(-25.37, -6.56) * mm});
            skLineSegment(sketch, "E157.MirrorCS", {"start": v(-36.3, 38.12) * mm, "end": v(-29.3, 38.12) * mm});
            skLineSegment(sketch, "E158.MirrorCS", {"start": v(-29.3, -12.87) * mm, "end": v(-36.3, -12.87) * mm});
            skLineSegment(sketch, "E159.MirrorCS", {"start": v(-25.8, 18.94) * mm, "end": v(-29.3, 25) * mm});
            skLineSegment(sketch, "E160.MirrorCS", {"start": v(-25.37, 31.31) * mm, "end": v(-28.87, 25.25) * mm});
            skLineSegment(sketch, "E161.MirrorCS", {"start": v(-18.37, -31.81) * mm, "end": v(-25.37, -31.81) * mm});
            skLineSegment(sketch, "E162.MirrorCS", {"start": v(-25.37, -6.56) * mm, "end": v(-28.87, -12.62) * mm});
            skLineSegment(sketch, "E163.MirrorCS", {"start": v(-29.3, -25.5) * mm, "end": v(-36.3, -25.5) * mm});
            skLineSegment(sketch, "E164.MirrorCS", {"start": v(-36.3, 50.25) * mm, "end": v(-39.8, 44.19) * mm});
            skLineSegment(sketch, "E165.MirrorCS", {"start": v(-25.8, 44.19) * mm, "end": v(-29.3, 50.25) * mm});
            skLineSegment(sketch, "E166.MirrorCS", {"start": v(-18.37, -18.69) * mm, "end": v(-14.87, -12.62) * mm});
            skLineSegment(sketch, "E167.MirrorCS", {"start": v(-39.8, -18.94) * mm, "end": v(-36.3, -25) * mm});
            skLineSegment(sketch, "E168.MirrorCS", {"start": v(-29.3, 0.25) * mm, "end": v(-25.8, 6.31) * mm});
            skLineSegment(sketch, "E169.MirrorCS", {"start": v(-14.87, 25.25) * mm, "end": v(-18.37, 31.31) * mm});
            skLineSegment(sketch, "E170.MirrorCS", {"start": v(-25.37, -43.94) * mm, "end": v(-18.37, -43.94) * mm});
            skLineSegment(sketch, "E171.MirrorCS", {"start": v(-36.3, -37.62) * mm, "end": v(-29.3, -37.62) * mm});
            skLineSegment(sketch, "E172.MirrorCS", {"start": v(-29.3, 12.37) * mm, "end": v(-36.3, 12.37) * mm});
            skLineSegment(sketch, "E173.MirrorCS", {"start": v(-29.3, -12.37) * mm, "end": v(-25.8, -6.31) * mm});
            skLineSegment(sketch, "E174.MirrorCS", {"start": v(-36.3, 37.62) * mm, "end": v(-39.8, 31.56) * mm});
            skLineSegment(sketch, "E175.MirrorCS", {"start": v(-28.87, 12.62) * mm, "end": v(-25.37, 6.56) * mm});
            skLineSegment(sketch, "E176.MirrorCS", {"start": v(-25.37, 18.69) * mm, "end": v(-28.87, 12.62) * mm});
            skLineSegment(sketch, "E177.MirrorCS", {"start": v(-14.87, 12.62) * mm, "end": v(-18.37, 18.69) * mm});
            skLineSegment(sketch, "E178.MirrorCS", {"start": v(-18.37, 6.56) * mm, "end": v(-14.87, 12.62) * mm});
            skLineSegment(sketch, "E179.MirrorCS", {"start": v(-25.37, 6.56) * mm, "end": v(-18.37, 6.56) * mm});
            skLineSegment(sketch, "E180.MirrorCS", {"start": v(-18.37, 18.69) * mm, "end": v(-25.37, 18.69) * mm});
            skLineSegment(sketch, "E181.MirrorCS", {"start": v(-18.37, -6.06) * mm, "end": v(-14.87, 0) * mm});
            skLineSegment(sketch, "E182.MirrorCS", {"start": v(-28.87, -37.87) * mm, "end": v(-25.37, -43.94) * mm});
            skLineSegment(sketch, "E183.MirrorCS", {"start": v(-39.8, -31.56) * mm, "end": v(-36.3, -37.62) * mm});
            skLineSegment(sketch, "E184.MirrorCS", {"start": v(-25.37, -6.06) * mm, "end": v(-18.37, -6.06) * mm});
            skLineSegment(sketch, "E185.MirrorCS", {"start": v(-28.87, 0) * mm, "end": v(-25.37, -6.06) * mm});
            skLineSegment(sketch, "E186.MirrorCS", {"start": v(-25.37, 6.06) * mm, "end": v(-28.87, 0) * mm});
            skLineSegment(sketch, "E187.MirrorCS", {"start": v(-29.3, 50.25) * mm, "end": v(-36.3, 50.25) * mm});
            skLineSegment(sketch, "E188.MirrorCS", {"start": v(-25.37, -18.69) * mm, "end": v(-18.37, -18.69) * mm});
            skLineSegment(sketch, "E189.MirrorCS", {"start": v(-18.37, 6.06) * mm, "end": v(-25.37, 6.06) * mm});
            skLineSegment(sketch, "E190.MirrorCS", {"start": v(-25.8, -18.94) * mm, "end": v(-29.3, -12.87) * mm});
            skLineSegment(sketch, "E191.MirrorCS", {"start": v(-36.3, 0.25) * mm, "end": v(-29.3, 0.25) * mm});
            skLineSegment(sketch, "E192.MirrorCS", {"start": v(-14.87, 0) * mm, "end": v(-18.37, 6.06) * mm});
            skLineSegment(sketch, "E193.MirrorCS", {"start": v(-18.37, 19.19) * mm, "end": v(-14.87, 25.25) * mm});
            skLineSegment(sketch, "E194.MirrorCS", {"start": v(-36.3, -12.37) * mm, "end": v(-29.3, -12.37) * mm});
            skLineSegment(sketch, "E195.MirrorCS", {"start": v(-29.3, 37.62) * mm, "end": v(-36.3, 37.62) * mm});
            skLineSegment(sketch, "E196.MirrorCS", {"start": v(-25.37, 19.19) * mm, "end": v(-18.37, 19.19) * mm});
            skLineSegment(sketch, "E197.MirrorCS", {"start": v(-25.37, -31.81) * mm, "end": v(-28.87, -37.87) * mm});
            skLineSegment(sketch, "E198.MirrorCS", {"start": v(-18.37, 31.31) * mm, "end": v(-25.37, 31.31) * mm});
            skLineSegment(sketch, "E199.MirrorCS", {"start": v(-25.8, -31.56) * mm, "end": v(-29.3, -25.5) * mm});
            skLineSegment(sketch, "E200.MirrorCS", {"start": v(-14.87, -12.62) * mm, "end": v(-18.37, -6.56) * mm});
            skLineSegment(sketch, "E201.MirrorCS", {"start": v(-18.37, -43.94) * mm, "end": v(-14.87, -37.87) * mm});
            skLineSegment(sketch, "E202.MirrorCS", {"start": v(-29.3, -37.62) * mm, "end": v(-25.8, -31.56) * mm});
            skLineSegment(sketch, "E203.MirrorCS", {"start": v(-36.3, 12.37) * mm, "end": v(-39.8, 6.31) * mm});
            skLineSegment(sketch, "E204.MirrorCS", {"start": v(-36.3, -0.25) * mm, "end": v(-39.8, -6.31) * mm});
            skLineSegment(sketch, "E205.MirrorCS", {"start": v(-39.8, 31.56) * mm, "end": v(-36.3, 25.5) * mm});
            skLineSegment(sketch, "E206.MirrorCS", {"start": v(-28.87, 37.87) * mm, "end": v(-25.37, 31.81) * mm});
            skLineSegment(sketch, "E207.MirrorCS", {"start": v(-29.3, -50.25) * mm, "end": v(-25.8, -44.19) * mm});
            skLineSegment(sketch, "E208.MirrorCS", {"start": v(-39.8, 6.31) * mm, "end": v(-36.3, 0.25) * mm});
            skLineSegment(sketch, "E209.MirrorCS", {"start": v(-29.3, 25.5) * mm, "end": v(-25.8, 31.56) * mm});
            skLineSegment(sketch, "E210.MirrorCS", {"start": v(-28.87, -12.62) * mm, "end": v(-25.37, -18.69) * mm});
            skLineSegment(sketch, "E211.MirrorCS", {"start": v(-14.87, -37.87) * mm, "end": v(-18.37, -31.81) * mm});
            skLineSegment(sketch, "E212.MirrorCS", {"start": v(-36.3, -25.5) * mm, "end": v(-39.8, -31.56) * mm});
            skLineSegment(sketch, "E213.MirrorCS", {"start": v(-39.8, 44.19) * mm, "end": v(-36.3, 38.12) * mm});
            skLineSegment(sketch, "E214.MirrorCS", {"start": v(-25.8, 6.31) * mm, "end": v(-29.3, 12.37) * mm});
            skLineSegment(sketch, "E215.MirrorCS", {"start": v(-36.3, 25.5) * mm, "end": v(-29.3, 25.5) * mm});
            skLineSegment(sketch, "E216.MirrorCS", {"start": v(-28.87, 25.25) * mm, "end": v(-25.37, 19.19) * mm});
            skLineSegment(sketch, "E217.MirrorCS", {"start": v(-39.8, 18.94) * mm, "end": v(-36.3, 12.87) * mm});
            skLineSegment(sketch, "E218.MirrorCS", {"start": v(-36.3, -12.87) * mm, "end": v(-39.8, -18.94) * mm});
            skLineSegment(sketch, "E219.MirrorCS", {"start": v(-25.37, -19.19) * mm, "end": v(-28.87, -25.25) * mm});
            skLineSegment(sketch, "E220.MirrorCS", {"start": v(-29.3, 38.12) * mm, "end": v(-25.8, 44.19) * mm});
            skLineSegment(sketch, "E221.MirrorCS", {"start": v(-29.3, 25) * mm, "end": v(-36.3, 25) * mm});
            skLineSegment(sketch, "E222.MirrorCS", {"start": v(-36.3, -25) * mm, "end": v(-29.3, -25) * mm});
            skLineSegment(sketch, "E223.MirrorCS", {"start": v(-25.8, -44.19) * mm, "end": v(-29.3, -38.12) * mm});
            skLineSegment(sketch, "E224.MirrorCS", {"start": v(-28.87, -25.25) * mm, "end": v(-25.37, -31.31) * mm});
            skLineSegment(sketch, "E225.MirrorCS", {"start": v(-25.37, -31.31) * mm, "end": v(-18.37, -31.31) * mm});
            skLineSegment(sketch, "E226.MirrorCS", {"start": v(-39.8, -44.19) * mm, "end": v(-36.3, -50.25) * mm});
            skLineSegment(sketch, "E227.MirrorCS", {"start": v(-39.8, -6.31) * mm, "end": v(-36.3, -12.37) * mm});
            skLineSegment(sketch, "E228.MirrorCS", {"start": v(-29.3, 12.87) * mm, "end": v(-25.8, 18.94) * mm});
            skLineSegment(sketch, "E229.MirrorCS", {"start": v(-14.87, 37.87) * mm, "end": v(-18.37, 43.94) * mm});
            skLineSegment(sketch, "E230.MirrorCS", {"start": v(-18.37, 43.94) * mm, "end": v(-25.37, 43.94) * mm});
            skLineSegment(sketch, "E231.MirrorCS", {"start": v(-14.87, -25.25) * mm, "end": v(-18.37, -19.19) * mm});
            skLineSegment(sketch, "E232.MirrorCS", {"start": v(-36.3, -38.12) * mm, "end": v(-39.8, -44.19) * mm});
            skLineSegment(sketch, "E233.MirrorCS", {"start": v(-25.8, -6.31) * mm, "end": v(-29.3, -0.25) * mm});
            skLineSegment(sketch, "E234.MirrorCS", {"start": v(-36.3, 12.87) * mm, "end": v(-29.3, 12.87) * mm});
            skLineSegment(sketch, "E235.MirrorCS", {"start": v(-18.37, 31.81) * mm, "end": v(-14.87, 37.87) * mm});
            skLineSegment(sketch, "E236.MirrorCS", {"start": v(-25.37, 31.81) * mm, "end": v(-18.37, 31.81) * mm});
            skLineSegment(sketch, "E237.MirrorCS", {"start": v(-36.3, 25) * mm, "end": v(-39.8, 18.94) * mm});
            skLineSegment(sketch, "E238.MirrorCS", {"start": v(-29.3, -25) * mm, "end": v(-25.8, -18.94) * mm});
            skLineSegment(sketch, "E239.MirrorCS", {"start": v(-18.37, -19.19) * mm, "end": v(-25.37, -19.19) * mm});
            skLineSegment(sketch, "E240.MirrorCS", {"start": v(-29.3, -38.12) * mm, "end": v(-36.3, -38.12) * mm});
            skLineSegment(sketch, "E241.MirrorCS", {"start": v(-25.8, 31.56) * mm, "end": v(-29.3, 37.62) * mm});
            skLineSegment(sketch, "E242.MirrorCS", {"start": v(-36.3, -50.25) * mm, "end": v(-29.3, -50.25) * mm});
            skLineSegment(sketch, "E243.MirrorCS", {"start": v(-29.3, -0.25) * mm, "end": v(-36.3, -0.25) * mm});
            skLineSegment(sketch, "E244.MirrorCS", {"start": v(-18.37, -31.31) * mm, "end": v(-14.87, -25.25) * mm});
            skLineSegment(sketch, "E245.MirrorCS", {"start": v(-25.37, 43.94) * mm, "end": v(-28.87, 37.87) * mm});
            skLineSegment(sketch, "E246", {"start": v(10.93, -53.54) * mm, "end": v(10.93, 52.1) * mm, "construction": true});
            skPoint(sketch, "E246.startSnap0", {"position": v(10.93, -50.25) * mm});
            skLineSegment(sketch, "E247.MirrorCS", {"start": v(39.8, -31.56) * mm, "end": v(36.3, -37.62) * mm});
            skLineSegment(sketch, "E248.MirrorCS", {"start": v(36.3, -25.5) * mm, "end": v(39.8, -31.56) * mm});
            skLineSegment(sketch, "E249.MirrorCS", {"start": v(36.3, 12.37) * mm, "end": v(39.8, 6.31) * mm});
            skLineSegment(sketch, "E250.MirrorCS", {"start": v(39.8, 44.19) * mm, "end": v(36.3, 38.12) * mm});
            skLineSegment(sketch, "E251.MirrorCS", {"start": v(36.3, 37.62) * mm, "end": v(39.8, 31.56) * mm});
            skLineSegment(sketch, "E252.MirrorCS", {"start": v(36.3, 25) * mm, "end": v(39.8, 18.94) * mm});
            skLineSegment(sketch, "E253.MirrorCS", {"start": v(39.8, 18.94) * mm, "end": v(36.3, 12.87) * mm});
            skLineSegment(sketch, "E254.MirrorCS", {"start": v(36.3, -38.12) * mm, "end": v(39.8, -44.19) * mm});
            skLineSegment(sketch, "E255.MirrorCS", {"start": v(36.3, -12.87) * mm, "end": v(39.8, -18.94) * mm});
            skLineSegment(sketch, "E256.MirrorCS", {"start": v(39.8, -18.94) * mm, "end": v(36.3, -25) * mm});
            skLineSegment(sketch, "E257.MirrorCS", {"start": v(36.3, -0.25) * mm, "end": v(39.8, -6.31) * mm});
            skLineSegment(sketch, "E258.MirrorCS", {"start": v(39.8, -6.31) * mm, "end": v(36.3, -12.37) * mm});
            skLineSegment(sketch, "E259.MirrorCS", {"start": v(39.8, -44.19) * mm, "end": v(36.3, -50.25) * mm});
            skLineSegment(sketch, "E260.MirrorCS", {"start": v(36.3, 50.25) * mm, "end": v(39.8, 44.19) * mm});
            skLineSegment(sketch, "E261.MirrorCS", {"start": v(39.8, 6.31) * mm, "end": v(36.3, 0.25) * mm});
            skLineSegment(sketch, "E262.MirrorCS", {"start": v(39.8, 31.56) * mm, "end": v(36.3, 25.5) * mm});
            skLineSegment(sketch, "E263.MirrorCS", {"start": v(18.37, 18.69) * mm, "end": v(14.87, 12.62) * mm});
            skLineSegment(sketch, "E264.MirrorCS", {"start": v(14.87, 0) * mm, "end": v(18.37, -6.06) * mm});
            skLineSegment(sketch, "E265.MirrorCS", {"start": v(18.37, 6.06) * mm, "end": v(14.87, 0) * mm});
            skLineSegment(sketch, "E266.MirrorCS", {"start": v(18.37, 43.94) * mm, "end": v(14.87, 37.87) * mm});
            skLineSegment(sketch, "E267.MirrorCS", {"start": v(14.87, 37.87) * mm, "end": v(18.37, 31.81) * mm});
            skLineSegment(sketch, "E268.MirrorCS", {"start": v(14.87, 12.62) * mm, "end": v(18.37, 6.56) * mm});
            skLineSegment(sketch, "E269.MirrorCS", {"start": v(18.37, -31.81) * mm, "end": v(14.87, -37.87) * mm});
            skLineSegment(sketch, "E270.MirrorCS", {"start": v(18.37, -6.56) * mm, "end": v(14.87, -12.62) * mm});
            skLineSegment(sketch, "E271.MirrorCS", {"start": v(14.87, -25.25) * mm, "end": v(18.37, -31.31) * mm});
            skLineSegment(sketch, "E272.MirrorCS", {"start": v(14.87, -37.87) * mm, "end": v(18.37, -43.94) * mm});
            skLineSegment(sketch, "E273.MirrorCS", {"start": v(14.87, 25.25) * mm, "end": v(18.37, 19.19) * mm});
            skLineSegment(sketch, "E274.MirrorCS", {"start": v(18.37, 31.31) * mm, "end": v(14.87, 25.25) * mm});
            skLineSegment(sketch, "E275.MirrorCS", {"start": v(18.37, -19.19) * mm, "end": v(14.87, -25.25) * mm});
            skLineSegment(sketch, "E276.MirrorCS", {"start": v(14.87, -12.62) * mm, "end": v(18.37, -18.69) * mm});
            skLineSegment(sketch, "E277.MirrorCS", {"start": v(24.47, -6.06) * mm, "end": v(24.57, -6.06) * mm, "construction": true});
            skLineSegment(sketch, "E278.MirrorCS", {"start": v(24.47, -43.94) * mm, "end": v(25.37, -43.94) * mm, "construction": true});
            skLineSegment(sketch, "E279.MirrorCS", {"start": v(24.47, -6.06) * mm, "end": v(25.37, -6.06) * mm, "construction": true});
            skLineSegment(sketch, "E280.MirrorCS", {"start": v(24.47, -18.69) * mm, "end": v(25.37, -18.69) * mm, "construction": true});
            skLineSegment(sketch, "E281.MirrorCS", {"start": v(24.47, -31.31) * mm, "end": v(25.37, -31.31) * mm, "construction": true});
            skLineSegment(sketch, "E282.MirrorCS", {"start": v(29.3, -0.25) * mm, "end": v(36.3, -0.25) * mm});
            skLineSegment(sketch, "E283.MirrorCS", {"start": v(36.3, 0.25) * mm, "end": v(29.3, 0.25) * mm});
            skLineSegment(sketch, "E284.MirrorCS", {"start": v(29.3, 50.25) * mm, "end": v(36.3, 50.25) * mm});
            skLineSegment(sketch, "E285.MirrorCS", {"start": v(36.3, -50.25) * mm, "end": v(29.3, -50.25) * mm});
            skLineSegment(sketch, "E286.MirrorCS", {"start": v(25.37, 6.56) * mm, "end": v(28.87, 12.62) * mm});
            skLineSegment(sketch, "E287.MirrorCS", {"start": v(18.37, 6.56) * mm, "end": v(25.37, 6.56) * mm});
            skLineSegment(sketch, "E288.MirrorCS", {"start": v(25.37, 18.69) * mm, "end": v(18.37, 18.69) * mm});
            skLineSegment(sketch, "E289.MirrorCS", {"start": v(25.37, -6.06) * mm, "end": v(28.87, 0) * mm});
            skLineSegment(sketch, "E290.MirrorCS", {"start": v(18.37, -6.06) * mm, "end": v(25.37, -6.06) * mm});
            skLineSegment(sketch, "E291.MirrorCS", {"start": v(36.3, 38.12) * mm, "end": v(29.3, 38.12) * mm});
            skLineSegment(sketch, "E292.MirrorCS", {"start": v(25.8, 31.56) * mm, "end": v(29.3, 37.62) * mm});
            skLineSegment(sketch, "E293.MirrorCS", {"start": v(29.3, -12.87) * mm, "end": v(36.3, -12.87) * mm});
            skLineSegment(sketch, "E294.MirrorCS", {"start": v(29.3, 25) * mm, "end": v(36.3, 25) * mm});
            skLineSegment(sketch, "E295.MirrorCS", {"start": v(29.3, 38.12) * mm, "end": v(25.8, 44.19) * mm});
            skLineSegment(sketch, "E296.MirrorCS", {"start": v(29.3, -38.12) * mm, "end": v(36.3, -38.12) * mm});
            skLineSegment(sketch, "E297.MirrorCS", {"start": v(18.37, -18.69) * mm, "end": v(25.37, -18.69) * mm});
            skLineSegment(sketch, "E298.MirrorCS", {"start": v(25.37, 6.06) * mm, "end": v(18.37, 6.06) * mm});
            skLineSegment(sketch, "E299.MirrorCS", {"start": v(25.37, -31.31) * mm, "end": v(28.87, -25.25) * mm});
            skLineSegment(sketch, "E300.MirrorCS", {"start": v(28.87, 0) * mm, "end": v(25.37, 6.06) * mm});
            skLineSegment(sketch, "E301.MirrorCS", {"start": v(25.8, -6.31) * mm, "end": v(29.3, -0.25) * mm});
            skLineSegment(sketch, "E302.MirrorCS", {"start": v(29.3, -37.62) * mm, "end": v(25.8, -31.56) * mm});
            skLineSegment(sketch, "E303.MirrorCS", {"start": v(18.37, -31.31) * mm, "end": v(25.37, -31.31) * mm});
            skLineSegment(sketch, "E304.MirrorCS", {"start": v(28.87, 37.87) * mm, "end": v(25.37, 43.94) * mm});
            skLineSegment(sketch, "E305.MirrorCS", {"start": v(29.3, -50.25) * mm, "end": v(25.8, -44.19) * mm});
            skLineSegment(sketch, "E306.MirrorCS", {"start": v(25.8, -18.94) * mm, "end": v(29.3, -12.87) * mm});
            skLineSegment(sketch, "E307.MirrorCS", {"start": v(25.37, -6.56) * mm, "end": v(18.37, -6.56) * mm});
            skLineSegment(sketch, "E308.MirrorCS", {"start": v(18.37, -43.94) * mm, "end": v(25.37, -43.94) * mm});
            skLineSegment(sketch, "E309.MirrorCS", {"start": v(25.37, 19.19) * mm, "end": v(28.87, 25.25) * mm});
            skLineSegment(sketch, "E310.MirrorCS", {"start": v(28.87, -25.25) * mm, "end": v(25.37, -19.19) * mm});
            skLineSegment(sketch, "E311.MirrorCS", {"start": v(25.37, 31.81) * mm, "end": v(28.87, 37.87) * mm});
            skLineSegment(sketch, "E312.MirrorCS", {"start": v(18.37, 19.19) * mm, "end": v(25.37, 19.19) * mm});
            skLineSegment(sketch, "E313.MirrorCS", {"start": v(36.3, -37.62) * mm, "end": v(29.3, -37.62) * mm});
            skLineSegment(sketch, "E314.MirrorCS", {"start": v(36.3, 12.87) * mm, "end": v(29.3, 12.87) * mm});
            skLineSegment(sketch, "E315.MirrorCS", {"start": v(18.37, 31.81) * mm, "end": v(25.37, 31.81) * mm});
            skLineSegment(sketch, "E316.MirrorCS", {"start": v(28.87, 12.62) * mm, "end": v(25.37, 18.69) * mm});
            skLineSegment(sketch, "E317.MirrorCS", {"start": v(29.3, -25) * mm, "end": v(25.8, -18.94) * mm});
            skLineSegment(sketch, "E318.MirrorCS", {"start": v(29.3, 37.62) * mm, "end": v(36.3, 37.62) * mm});
            skLineSegment(sketch, "E319.MirrorCS", {"start": v(29.3, 12.37) * mm, "end": v(36.3, 12.37) * mm});
            skLineSegment(sketch, "E320.MirrorCS", {"start": v(28.87, 25.25) * mm, "end": v(25.37, 31.31) * mm});
            skLineSegment(sketch, "E321.MirrorCS", {"start": v(25.37, -18.69) * mm, "end": v(28.87, -12.62) * mm});
            skLineSegment(sketch, "E322.MirrorCS", {"start": v(36.3, -12.37) * mm, "end": v(29.3, -12.37) * mm});
            skLineSegment(sketch, "E323.MirrorCS", {"start": v(25.8, 44.19) * mm, "end": v(29.3, 50.25) * mm});
            skLineSegment(sketch, "E324.MirrorCS", {"start": v(25.37, -19.19) * mm, "end": v(18.37, -19.19) * mm});
            skLineSegment(sketch, "E325.MirrorCS", {"start": v(25.37, -31.81) * mm, "end": v(18.37, -31.81) * mm});
            skLineSegment(sketch, "E326.MirrorCS", {"start": v(25.37, 31.31) * mm, "end": v(18.37, 31.31) * mm});
            skLineSegment(sketch, "E327.MirrorCS", {"start": v(29.3, 12.87) * mm, "end": v(25.8, 18.94) * mm});
            skLineSegment(sketch, "E328.MirrorCS", {"start": v(25.8, 6.31) * mm, "end": v(29.3, 12.37) * mm});
            skLineSegment(sketch, "E329.MirrorCS", {"start": v(29.3, -25.5) * mm, "end": v(36.3, -25.5) * mm});
            skLineSegment(sketch, "E330.MirrorCS", {"start": v(29.3, 0.25) * mm, "end": v(25.8, 6.31) * mm});
            skLineSegment(sketch, "E331.MirrorCS", {"start": v(25.37, 43.94) * mm, "end": v(18.37, 43.94) * mm});
            skLineSegment(sketch, "E332.MirrorCS", {"start": v(36.3, -25) * mm, "end": v(29.3, -25) * mm});
            skLineSegment(sketch, "E333.MirrorCS", {"start": v(25.8, -44.19) * mm, "end": v(29.3, -38.12) * mm});
            skLineSegment(sketch, "E334.MirrorCS", {"start": v(25.8, 18.94) * mm, "end": v(29.3, 25) * mm});
            skLineSegment(sketch, "E335.MirrorCS", {"start": v(29.3, 25.5) * mm, "end": v(25.8, 31.56) * mm});
            skLineSegment(sketch, "E336.MirrorCS", {"start": v(29.3, -12.37) * mm, "end": v(25.8, -6.31) * mm});
            skLineSegment(sketch, "E337.MirrorCS", {"start": v(25.37, -43.94) * mm, "end": v(28.87, -37.87) * mm});
            skLineSegment(sketch, "E338.MirrorCS", {"start": v(25.8, -31.56) * mm, "end": v(29.3, -25.5) * mm});
            skLineSegment(sketch, "E339.MirrorCS", {"start": v(36.3, 25.5) * mm, "end": v(29.3, 25.5) * mm});
            skLineSegment(sketch, "E340.MirrorCS", {"start": v(28.87, -12.62) * mm, "end": v(25.37, -6.56) * mm});
            skLineSegment(sketch, "E341.MirrorCS", {"start": v(28.87, -37.87) * mm, "end": v(25.37, -31.81) * mm});
            skSolve(sketch);
        }
        {
            var Q0;
            Q0=makeQuery(id+"F9.imprint","IMPRINT",FACE,{"disambiguationData":[TD([[makeQuery(id+"F9.imprint","IMPRINT",EDGE,{"derivedFrom":sQuery(id+"F9.wireOp",EDGE,"E74")}),-1.0]])]});
            var Q1;
            {var subQ0=sQuery(id+"F9.wireOp",EDGE,"E93");Q1=makeQuery(id+"F9.imprint","IMPRINT",FACE,{"disambiguationData":[TD([[makeQuery(id+"F9.imprint","IMPRINT",EDGE,{"derivedFrom":subQ0}),-1.0]])]});}
            var Q2;
            {var subQ0=sQuery(id+"F9.wireOp",EDGE,"E94");Q2=makeQuery(id+"F9.imprint","IMPRINT",FACE,{"disambiguationData":[TD([[makeQuery(id+"F9.imprint","IMPRINT",EDGE,{"derivedFrom":subQ0}),-1.0]])]});}
            var Q3;
            {var subQ1=sQuery(id+"F9.wireOp",EDGE,"E83.MirrorCS");Q3=makeQuery(id+"F9.imprint","IMPRINT",FACE,{"disambiguationData":[TD([[makeQuery(id+"F9.imprint","IMPRINT",EDGE,{"derivedFrom":subQ1}),1.0]])]});}
            var Q4;
            {var subQ1=sQuery(id+"F9.wireOp",EDGE,"E81");Q4=makeQuery(id+"F9.imprint","IMPRINT",FACE,{"disambiguationData":[TD([[makeQuery(id+"F9.imprint","IMPRINT",EDGE,{"derivedFrom":subQ1}),-1.0]])]});}
            var Q5;
            {var subQ4=sQuery(id+"F9.wireOp",EDGE,"E74");Q5=makeQuery(id+"F9.imprint","IMPRINT",FACE,{"disambiguationData":[TD([[makeQuery(id+"F9.imprint","IMPRINT",EDGE,{"derivedFrom":subQ4}),1.0]])]});}
            var Q6;
            {var subQ0=sQuery(id+"F9.wireOp",EDGE,"E86.MirrorCS");Q6=makeQuery(id+"F9.imprint","IMPRINT",FACE,{"disambiguationData":[TD([[makeQuery(id+"F9.imprint","IMPRINT",EDGE,{"derivedFrom":subQ0}),-1.0]])]});}
            extrude(context, id + "F11", {"entities" : qUnion([Q0, Q1, Q2, Q3, Q4, Q5, Q6]), "depth" : 14.2 * mm, "hasSecondDirection" : true, "secondDirectionOppositeDirection" : false, "secondDirectionDepth" : 9 * mm});
        }
        {
            var Q0;
            Q0 = qSketchRegion(id + "F10", true);
            extrude(context, id + "F12", {"entities" : qUnion([Q0]), "operationType" : NewBodyOperationType.REMOVE, "depth" : 25 * mm});
        }
        {
            var Q0;
            {var subQ4=sQuery(id+"F9.wireOp",EDGE,"E74");Q0=makeQuery(id+"F9.imprint","IMPRINT",FACE,{"disambiguationData":[TD([[makeQuery(id+"F9.imprint","IMPRINT",EDGE,{"derivedFrom":subQ4}),1.0]])]});}
            var Q1;
            {var subQ0=sQuery(id+"F9.wireOp",EDGE,"E86.MirrorCS");Q1=makeQuery(id+"F9.imprint","IMPRINT",FACE,{"disambiguationData":[TD([[makeQuery(id+"F9.imprint","IMPRINT",EDGE,{"derivedFrom":subQ0}),-1.0]])]});}
            extrude(context, id + "F13", {"entities" : qUnion([Q0, Q1]), "operationType" : NewBodyOperationType.ADD, "depth" : 14.2 * mm, "hasSecondDirection" : true, "secondDirectionOppositeDirection" : false, "secondDirectionDepth" : 9 * mm});
        }
        {
            var Q0;
            {var subQ4=sQuery(id+"F8.wireOp",EDGE,"E67");Q0=makeQuery(id+"F8.imprint","IMPRINT",FACE,{"disambiguationData":[TD([[makeQuery(id+"F8.imprint","IMPRINT",EDGE,{"derivedFrom":subQ4}),1.0]])]});}
            var Q1;
            Q1=sQuery(id+"F8.wireOp",EDGE,"E73");
            revolve(context, id + "F14", {"operationType" : NewBodyOperationType.REMOVE, "entities" : qUnion([Q0]), "axis" : qUnion([Q1]), "revolveType" : RevolveType.FULL, "oppositeDirection" : true});
        }
        {
            var Q0;
            Q0=makeQuery(id+"F6.imprint","IMPRINT",FACE,{"disambiguationData":[TD([[makeQuery(id+"F6.imprint","IMPRINT",EDGE,{"derivedFrom":sQuery(id+"F6.wireOp",EDGE,"E45.bottom")}),1.0]])]});
            var Q1;
            Q1=makeQuery(id+"F6.imprint","IMPRINT",FACE,{"disambiguationData":[TD([[makeQuery(id+"F6.imprint","IMPRINT",EDGE,{"derivedFrom":sQuery(id+"F6.wireOp",EDGE,"E24")}),1.0]])]});
            var Q2;
            Q2=makeQuery(id+"F6.imprint","IMPRINT",FACE,{"disambiguationData":[TD([[makeQuery(id+"F6.imprint","IMPRINT",EDGE,{"derivedFrom":sQuery(id+"F6.wireOp",EDGE,"E25")}),1.0]])]});
            var Q3;
            Q3=makeQuery(id+"F6.imprint","IMPRINT",FACE,{"disambiguationData":[TD([[makeQuery(id+"F6.imprint","IMPRINT",EDGE,{"derivedFrom":sQuery(id+"F6.wireOp",EDGE,"E26")}),1.0]])]});
            var Q4;
            Q4=makeQuery(id+"F6.imprint","IMPRINT",FACE,{"disambiguationData":[TD([[makeQuery(id+"F6.imprint","IMPRINT",EDGE,{"derivedFrom":sQuery(id+"F6.wireOp",EDGE,"E23")}),1.0]])]});
            extrude(context, id + "F15", {"entities" : qUnion([Q0, Q1, Q2, Q3, Q4]), "operationType" : NewBodyOperationType.REMOVE, "depth" : 25 * mm});
        }
        {
            var Q0;
            Q0=makeQuery(id+"F6.imprint","IMPRINT",FACE,{"disambiguationData":[TD([[makeQuery(id+"F6.imprint","IMPRINT",EDGE,{"derivedFrom":sQuery(id+"F6.wireOp",EDGE,"E24")}),-1.0]])]});
            var Q1;
            {var subQ0=sQuery(id+"F6.wireOp",EDGE,"E50");var subQ1=sQuery(id+"F6.wireOp",EDGE,"E37");var subQ2=makeQuery(id+"F6.imprint","INTERSECT",VERTEX,{"disambiguationData":[OD(0.0)],"derivedFrom":[subQ1,subQ0]});Q1=makeQuery(id+"F6.imprint","IMPRINT",FACE,{"disambiguationData":[TD([[makeQuery(id+"F6.imprint","IMPRINT",EDGE,{"disambiguationData":[TD([[subQ2,-1.0]])],"derivedFrom":subQ1}),1.0]])]});}
            var Q2;
            Q2=makeQuery(id+"F6.imprint","IMPRINT",FACE,{"disambiguationData":[TD([[makeQuery(id+"F6.imprint","IMPRINT",EDGE,{"derivedFrom":sQuery(id+"F6.wireOp",EDGE,"E25")}),-1.0]])]});
            var Q3;
            {var subQ0=sQuery(id+"F6.wireOp",EDGE,"E53");var subQ1=sQuery(id+"F6.wireOp",EDGE,"E34");var subQ2=makeQuery(id+"F6.imprint","INTERSECT",VERTEX,{"disambiguationData":[OD(0.0)],"derivedFrom":[subQ1,subQ0]});Q3=makeQuery(id+"F6.imprint","IMPRINT",FACE,{"disambiguationData":[TD([[makeQuery(id+"F6.imprint","IMPRINT",EDGE,{"disambiguationData":[TD([[subQ2,-1.0]])],"derivedFrom":subQ1}),-1.0]])]});}
            var Q4;
            Q4=makeQuery(id+"F6.imprint","IMPRINT",FACE,{"disambiguationData":[TD([[makeQuery(id+"F6.imprint","IMPRINT",EDGE,{"derivedFrom":sQuery(id+"F6.wireOp",EDGE,"E26")}),-1.0]])]});
            var Q5;
            {var subQ0=sQuery(id+"F6.wireOp",EDGE,"E52");var subQ1=sQuery(id+"F6.wireOp",EDGE,"E40");var subQ2=makeQuery(id+"F6.imprint","INTERSECT",VERTEX,{"disambiguationData":[OD(0.0)],"derivedFrom":[subQ1,subQ0]});Q5=makeQuery(id+"F6.imprint","IMPRINT",FACE,{"disambiguationData":[TD([[makeQuery(id+"F6.imprint","IMPRINT",EDGE,{"disambiguationData":[TD([[subQ2,-1.0]])],"derivedFrom":subQ1}),-1.0]])]});}
            var Q6;
            Q6=makeQuery(id+"F6.imprint","IMPRINT",FACE,{"disambiguationData":[TD([[makeQuery(id+"F6.imprint","IMPRINT",EDGE,{"derivedFrom":sQuery(id+"F6.wireOp",EDGE,"E23")}),-1.0]])]});
            var Q7;
            {var subQ0=sQuery(id+"F6.wireOp",EDGE,"E51");var subQ1=sQuery(id+"F6.wireOp",EDGE,"E43");var subQ2=makeQuery(id+"F6.imprint","INTERSECT",VERTEX,{"disambiguationData":[OD(0.0)],"derivedFrom":[subQ1,subQ0]});Q7=makeQuery(id+"F6.imprint","IMPRINT",FACE,{"disambiguationData":[TD([[makeQuery(id+"F6.imprint","IMPRINT",EDGE,{"disambiguationData":[TD([[subQ2,-1.0]])],"derivedFrom":subQ1}),1.0]])]});}
            extrude(context, id + "F16", {"entities" : qUnion([Q0, Q1, Q2, Q3, Q4, Q5, Q6, Q7]), "operationType" : NewBodyOperationType.REMOVE, "depth" : 30 * mm, "hasSecondDirection" : true, "secondDirectionOppositeDirection" : false, "secondDirectionDepth" : 9.5 * mm});
        }
        {
            var Q0;
            {var subQ0=sQuery(id+"F9.wireOp",EDGE,"E93");Q0=makeQuery(id+"F9.imprint","IMPRINT",FACE,{"disambiguationData":[TD([[makeQuery(id+"F9.imprint","IMPRINT",EDGE,{"derivedFrom":subQ0}),-1.0]])]});}
            var Q1;
            {var subQ0=sQuery(id+"F9.wireOp",EDGE,"E94");Q1=makeQuery(id+"F9.imprint","IMPRINT",FACE,{"disambiguationData":[TD([[makeQuery(id+"F9.imprint","IMPRINT",EDGE,{"derivedFrom":subQ0}),-1.0]])]});}
            extrude(context, id + "F17", {"entities" : qUnion([Q0, Q1]), "operationType" : NewBodyOperationType.ADD, "depth" : 12 * mm, "hasSecondDirection" : true, "secondDirectionOppositeDirection" : false, "secondDirectionDepth" : 9 * mm});
        }
    });
